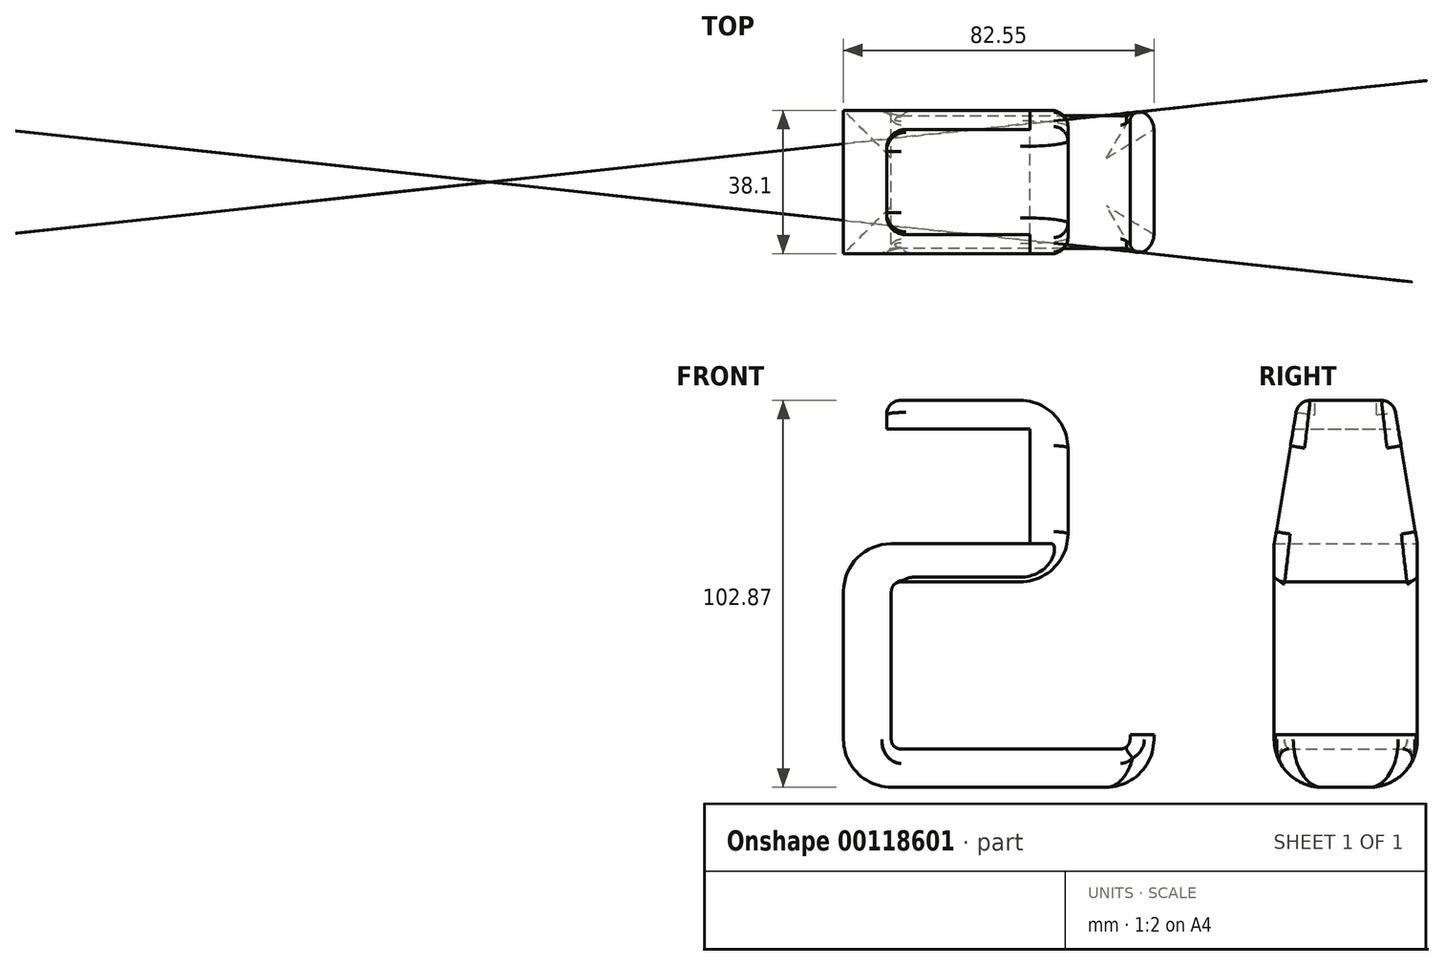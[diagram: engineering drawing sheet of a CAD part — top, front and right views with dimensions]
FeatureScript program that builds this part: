
annotation { "Feature Type Name" : "Feature", "Feature Type Description" : "" }
export const myFeature = defineFeature(function(context is Context, id is Id, definition is map)
    precondition{}
    {
        {
            var Q0;
            Q0=qCreatedBy(makeId("Front.planeOp"),FACE);
            var sketch = newSketch(context, id + "F0", { "sketchPlane" : qUnion([Q0])});
            skLineSegment(sketch, "E0", {"start": v(0, 0) * mm, "end": v(49.53, 0) * mm});
            skLineSegment(sketch, "E1", {"start": v(49.53, 0) * mm, "end": v(49.53, 30.48) * mm});
            skLineSegment(sketch, "E2", {"start": v(49.53, 30.48) * mm, "end": v(11.43, 30.48) * mm});
            skLineSegment(sketch, "E3", {"start": v(11.43, 38.1) * mm, "end": v(59.69, 38.1) * mm});
            skLineSegment(sketch, "E4", {"start": v(59.69, 38.1) * mm, "end": v(59.69, -10.16) * mm});
            skLineSegment(sketch, "E5", {"start": v(59.69, -10.16) * mm, "end": v(12.7, -10.16) * mm});
            skLineSegment(sketch, "E6", {"start": v(12.7, -10.16) * mm, "end": v(12.7, -54.61) * mm});
            skLineSegment(sketch, "E7", {"start": v(12.7, -54.61) * mm, "end": v(76.2, -54.6) * mm});
            skLineSegment(sketch, "E8", {"start": v(76.2, -54.6) * mm, "end": v(76.2, -50.8) * mm});
            skLineSegment(sketch, "E9", {"start": v(76.2, -50.8) * mm, "end": v(82.55, -50.8) * mm});
            skLineSegment(sketch, "E10", {"start": v(82.55, -50.8) * mm, "end": v(82.55, -64.77) * mm});
            skLineSegment(sketch, "E11", {"start": v(82.55, -64.77) * mm, "end": v(0, -64.77) * mm});
            skLineSegment(sketch, "E12", {"start": v(0, -64.77) * mm, "end": v(0, 0) * mm});
            skLineSegment(sketch, "E13", {"start": v(11.43, 38.1) * mm, "end": v(11.43, 30.48) * mm});
            skPoint(sketch, "E14.orphan", {"position": v(0, 30.48) * mm});
            skSolve(sketch);
        }
        {
            var Q0;
            Q0 = qSketchRegion(id + "F0", true);
            extrude(context, id + "F1", {"entities" : qUnion([Q0]), "endBound" : BoundingType.SYMMETRIC, "depth" : 38.1 * mm});
        }
        {
            var Q0;
            Q0=makeQuery(id+"F1.opExtrude","SWEPT_FACE",FACE,{"disambiguationData":[OSD([sQuery(id+"F0.wireOp",EDGE,"E4")])]});
            var sketch = newSketch(context, id + "F2", { "sketchPlane" : qUnion([Q0])});
            skLineSegment(sketch, "E15", {"start": v(-19.05, 0) * mm, "end": v(0, 114.3) * mm});
            skLineSegment(sketch, "E16", {"start": v(0, 114.3) * mm, "end": v(19.05, 0) * mm});
            skLineSegment(sketch, "E17", {"start": v(19.05, 0) * mm, "end": v(19.05, 139.7) * mm});
            skLineSegment(sketch, "E18", {"start": v(19.05, 139.7) * mm, "end": v(-19.05, 139.7) * mm});
            skLineSegment(sketch, "E19", {"start": v(-19.05, 139.7) * mm, "end": v(-19.05, 0) * mm});
            skSolve(sketch);
        }
        {
            var Q0;
            Q0 = qSketchRegion(id + "F2", true);
            extrude(context, id + "F3", {"entities" : qUnion([Q0]), "operationType" : NewBodyOperationType.REMOVE, "endBound" : BoundingType.THROUGH_ALL, "oppositeDirection" : true, "depth" : 25.4 * mm});
        }
        {
            var Q0;
            Q0 = qSketchRegion(id + "F2", true);
            extrude(context, id + "F4", {"entities" : qUnion([Q0]), "operationType" : NewBodyOperationType.REMOVE, "endBound" : BoundingType.THROUGH_ALL, "oppositeDirection" : true, "depth" : 25.4 * mm});
        }
        {
            var Q0;
            Q0=makeQuery(id+"F1.opExtrude","CAP_EDGE",EDGE,{"disambiguationData":[OSD([sQuery(id+"F0.wireOp",EDGE,"E10")])],"isStart":false});
            var Q1;
            Q1=makeQuery(id+"F1.opExtrude","CAP_EDGE",EDGE,{"disambiguationData":[OSD([sQuery(id+"F0.wireOp",EDGE,"E10")])],"isStart":true});
            fillet(context, id + "F5", {"entities" : qUnion([Q0, Q1]), "radius" : 5.08 * mm, "tangentPropagation" : true, "allowEdgeOverflow" : false});
        }
        {
            var Q0;
            Q0=makeQuery(id+"F1.opExtrude","SWEPT_EDGE",EDGE,{"disambiguationData":[OSD([sQuery(id+"F0.wireOp",EDGE,"E3"),sQuery(id+"F0.wireOp",EDGE,"E4")])]});
            var Q1;
            Q1=makeQuery(id+"F1.opExtrude","SWEPT_EDGE",EDGE,{"disambiguationData":[OSD([sQuery(id+"F0.wireOp",EDGE,"E4"),sQuery(id+"F0.wireOp",EDGE,"E5")])]});
            var Q2;
            Q2=makeQuery(id+"F1.opExtrude","SWEPT_EDGE",EDGE,{"disambiguationData":[OSD([sQuery(id+"F0.wireOp",EDGE,"E10"),sQuery(id+"F0.wireOp",EDGE,"E11")])]});
            var Q3;
            Q3=makeQuery(id+"F1.opExtrude","SWEPT_EDGE",EDGE,{"disambiguationData":[OSD([sQuery(id+"F0.wireOp",EDGE,"E0"),sQuery(id+"F0.wireOp",EDGE,"E12")])]});
            var Q4;
            Q4=makeQuery(id+"F1.opExtrude","SWEPT_EDGE",EDGE,{"disambiguationData":[OSD([sQuery(id+"F0.wireOp",EDGE,"E11"),sQuery(id+"F0.wireOp",EDGE,"E12")])]});
            fillet(context, id + "F6", {"entities" : qUnion([Q0, Q1, Q2, Q3, Q4]), "radius" : 12.7 * mm, "tangentPropagation" : true, "allowEdgeOverflow" : false});
        }
        {
            var Q0;
            Q0=makeQuery(id+"F3.boolean.opBoolean","INTERSECT",EDGE,{"derivedFrom":[makeQuery(id+"F1.opExtrude","SWEPT_FACE",FACE,{"disambiguationData":[OSD([sQuery(id+"F0.wireOp",EDGE,"E13")])]}),makeQuery(id+"F3.opExtrude","SWEPT_FACE",FACE,{"disambiguationData":[OSD([sQuery(id+"F2.wireOp",EDGE,"E15")])]})]});
            var Q1;
            Q1=makeQuery(id+"F3.boolean.opBoolean","INTERSECT",EDGE,{"derivedFrom":[makeQuery(id+"F1.opExtrude","SWEPT_FACE",FACE,{"disambiguationData":[OSD([sQuery(id+"F0.wireOp",EDGE,"E13")])]}),makeQuery(id+"F3.opExtrude","SWEPT_FACE",FACE,{"disambiguationData":[OSD([sQuery(id+"F2.wireOp",EDGE,"E16")])]})]});
            fillet(context, id + "F7", {"entities" : qUnion([Q0, Q1]), "radius" : 5.08 * mm, "tangentPropagation" : true, "allowEdgeOverflow" : false});
        }
        {
            var Q0;
            Q0=makeQuery(id+"F1.opExtrude","SWEPT_EDGE",EDGE,{"disambiguationData":[OSD([sQuery(id+"F0.wireOp",EDGE,"E5"),sQuery(id+"F0.wireOp",EDGE,"E6")])]});
            var Q1;
            Q1=makeQuery(id+"F1.opExtrude","SWEPT_EDGE",EDGE,{"disambiguationData":[OSD([sQuery(id+"F0.wireOp",EDGE,"E6"),sQuery(id+"F0.wireOp",EDGE,"E7")])]});
            var Q2;
            Q2=makeQuery(id+"F1.opExtrude","SWEPT_EDGE",EDGE,{"disambiguationData":[OSD([sQuery(id+"F0.wireOp",EDGE,"E7"),sQuery(id+"F0.wireOp",EDGE,"E8")])]});
            fillet(context, id + "F8", {"entities" : qUnion([Q0, Q1, Q2]), "radius" : 2.54 * mm, "tangentPropagation" : true, "allowEdgeOverflow" : false});
        }
        {
            var Q0;
            Q0=makeQuery(id+"F1.opExtrude","SWEPT_FACE",FACE,{"disambiguationData":[OSD([sQuery(id+"F0.wireOp",EDGE,"E3")])]});
            fillet(context, id + "F9", {"entities" : qUnion([Q0]), "radius" : 3.8 * mm, "tangentPropagation" : true, "allowEdgeOverflow" : false});
        }
        {
            var Q0;
            Q0=makeQuery(id+"F6.opFillet","BLEND_EDGE",EDGE,{"blendedFrom":[makeQuery(id+"F1.opExtrude","CAP_EDGE",EDGE,{"disambiguationData":[OSD([sQuery(id+"F0.wireOp",EDGE,"E11")])],"isStart":false}),makeQuery(id+"F1.opExtrude","SWEPT_FACE",FACE,{"disambiguationData":[OSD([sQuery(id+"F0.wireOp",EDGE,"E7")])]})],"blendedInto":[makeQuery(id+"F1.opExtrude","SWEPT_FACE",FACE,{"disambiguationData":[OSD([sQuery(id+"F0.wireOp",EDGE,"E7")])]})]});
            var Q1;
            Q1=makeQuery(id+"F6.opFillet","BLEND_EDGE",EDGE,{"blendedFrom":[makeQuery(id+"F1.opExtrude","CAP_EDGE",EDGE,{"disambiguationData":[OSD([sQuery(id+"F0.wireOp",EDGE,"E11")])],"isStart":true}),makeQuery(id+"F1.opExtrude","SWEPT_FACE",FACE,{"disambiguationData":[OSD([sQuery(id+"F0.wireOp",EDGE,"E7")])]})],"blendedInto":[makeQuery(id+"F1.opExtrude","SWEPT_FACE",FACE,{"disambiguationData":[OSD([sQuery(id+"F0.wireOp",EDGE,"E7")])]})]});
            fillet(context, id + "F10", {"entities" : qUnion([Q0, Q1]), "radius" : 2.54 * mm, "tangentPropagation" : true, "allowEdgeOverflow" : false});
        }
    });
